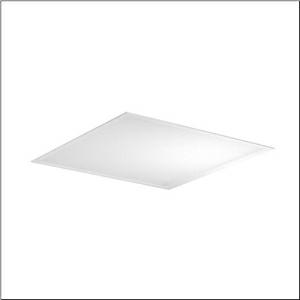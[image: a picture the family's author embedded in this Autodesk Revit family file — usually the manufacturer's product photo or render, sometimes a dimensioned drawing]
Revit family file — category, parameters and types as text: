
# Revit family: apollon_31_square_51mp12w72442
name_source: partatom
category: Lighting Fixtures
units: mm (PartAtom-declared; Revit-internal decimal feet)

## family parameters
Cut with Voids When Loaded = No
Host = Face
Light Source = No
Part Type = Normal
Room Calculation Point = No
Round Connector Dimension = Use Diameter
Shared = No

## types (1)
- Apollon 31 square (1 x LED, 4000 lm, 27.5 W, 4000K)
    Apparent Load = 28 VA
    CIE Flux Codes = 61 87 97 100 100
    Color Rendering = 80
    Color Temperature = 4000K
    Default Elevation = 1800 mm
    Description = Apollon 31 square, office luminaire, primary optical cover: micro prismatic cover, of PMMA, CAT 2 (L<= 3000cd/m²), light emission: direct distribution, primary light characteristic: symmetric, installation type: lay-in mounting, recessed, LED, rated luminous flux: 4.000lm, luminous efficacy: 145lm/W, light colour: 840, colour temperature: 4000K, control gear: ON/OFF, with terminal, 3-pole, mains connection: 220..240V, AC, 50/60Hz, rated input power: 28W, suitable for self-contained emergency lighting element 58DB00B013A with integrated self-test function according to EN 60598-2-22, housing, of aluminium, coated, traffic white (RAL 9016), module: M600, length: 595mm, width: 595mm, height: 62mm, housing upper side, of sheet steel, coated, protection rating (complete): IP20, protection rating (lamp compartment, on room side): IP40, insulation class (complete): insulation class II (safety insulation), certification: CE, ENEC, impact resistance: IK03, permissible operating ambient temperature: -20..+40°C, standard: EN 60598-2-22, corresponds to IFS (International Featured Standards) requirements for safety and quality in the food industry, packaging unit: 1 piece
    Height = 0 mm  [stored 0 ft]
    Lamp = 1 x LED
    Lamp Light Flux = 4000 lm
    Lamp Power = 27.5 W
    Lamp count = 1
    Length = 595 mm
    Luminous efficacy = 145 lm/W
    Manufacturer = Siteco
    ModVariant = No
    Model = 51MP12W72442
    Mounting Place = Ceiling
    Mounting Type = Recessed
    Number of Poles = 1
    OnlyDefault = Yes
    Power Factor = 1
    Product Name = Apollon 31 square
    Product group = office luminaire | ceiling recessed
    ProductGroupID = 400
    Protection Class = Protection class II
    Protection Degree = IP 20
    RLX_Detail_Level = 1
    RLX_Emergency_Light_Flux = 0 lm
    RLX_Emergency_Type = 0
    RLX_Emergency_Type_DB = No
    RlxData = <blob elided: 12837 chars, md5=9713b095>
    Socket = socket
    Standby Power = 0 W
    System Light Flux = 4000 lm
    System Power = 28 W
    Type Comments = Product without accessories
    Type Image = l_1291035.jpg
    URL = http://relux.com
    VarID = ---
    Voltage = 0 V
    Weight = 0.00 kg
    Width = 595 mm

note: [stored X ft] marks values corroborated as IEEE doubles in the binary element streams (Revit-internal decimal feet)

## geometry (parser evidence)
native form markers: Sweep x10
no freeform markers — native parametric forms only
